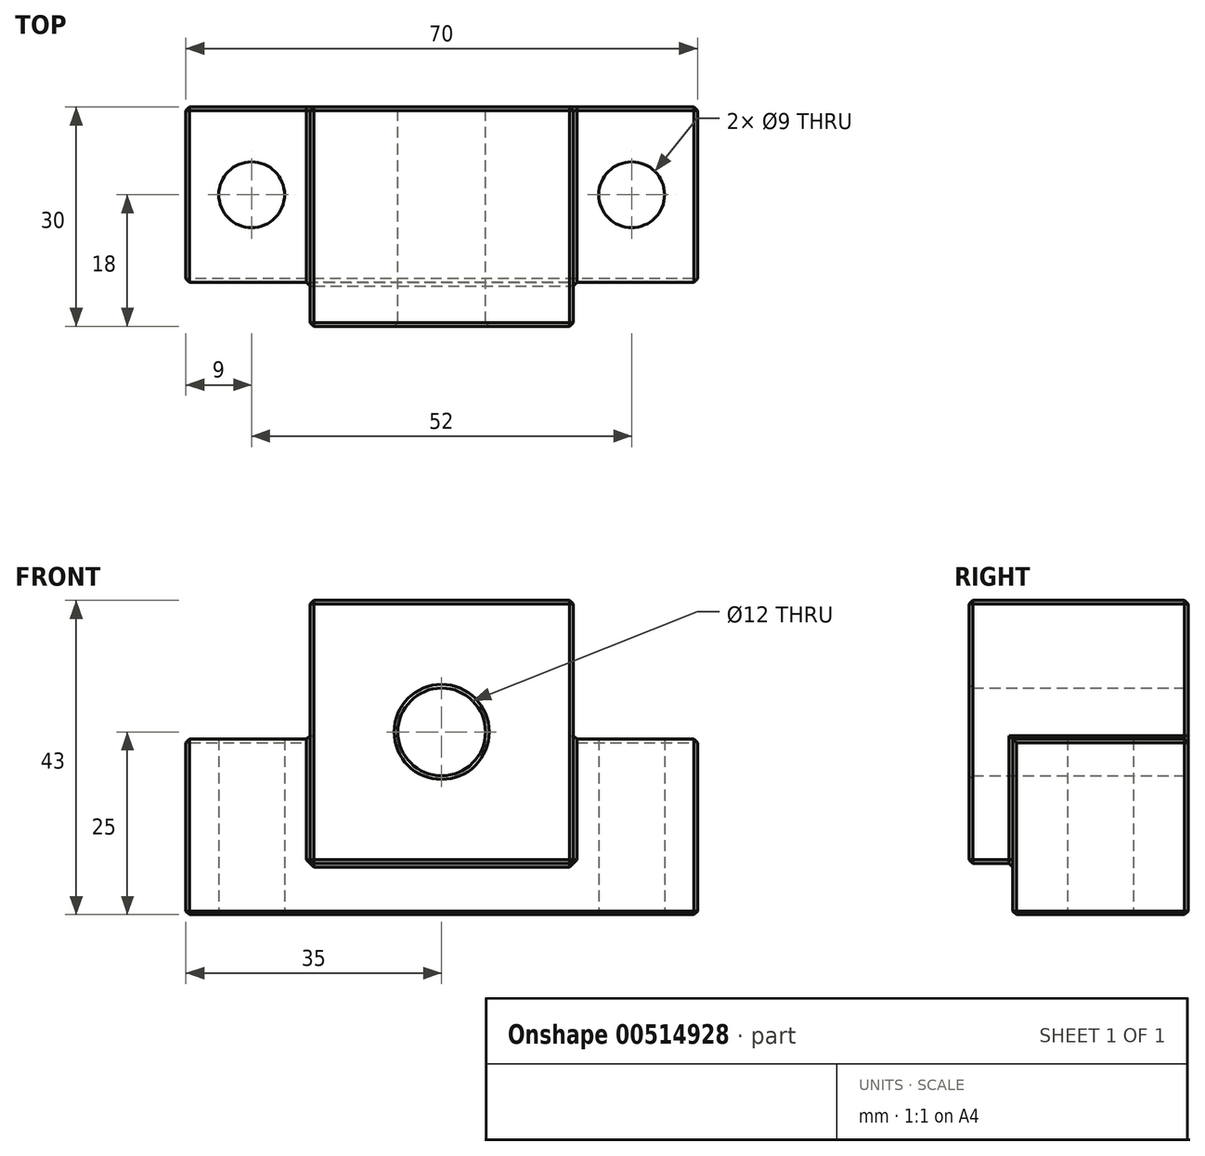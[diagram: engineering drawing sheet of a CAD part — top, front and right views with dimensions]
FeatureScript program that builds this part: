
annotation { "Feature Type Name" : "Feature", "Feature Type Description" : "" }
export const myFeature = defineFeature(function(context is Context, id is Id, definition is map)
    precondition{}
    {
        {
            var Q0;
            Q0=qCreatedBy(makeId("Front.planeOp"),FACE);
            var sketch = newSketch(context, id + "F0", { "sketchPlane" : qUnion([Q0])});
            skCircle(sketch, "E0", {"center": v(0, 0) * mm, "radius": 6 * mm});
            skLineSegment(sketch, "E1", {"start": v(0, 18) * mm, "end": v(18, 18) * mm});
            skLineSegment(sketch, "E2", {"start": v(18, 18) * mm, "end": v(18, -1) * mm});
            skLineSegment(sketch, "E3", {"start": v(18, -1) * mm, "end": v(35, -1) * mm});
            skLineSegment(sketch, "E4", {"start": v(35, -1) * mm, "end": v(35, -25) * mm});
            skLineSegment(sketch, "E5", {"start": v(35, -25) * mm, "end": v(0, -25) * mm});
            skLineSegment(sketch, "E6", {"start": v(0, 33.37) * mm, "end": v(0, -25.28) * mm, "construction": true});
            skCircle(sketch, "E7", {"center": v(0, 0) * mm, "radius": 9.5 * mm, "construction": true});
            skLineSegment(sketch, "E8.MirrorCS", {"start": v(0, 18) * mm, "end": v(-18, 18) * mm});
            skLineSegment(sketch, "E9.MirrorCS", {"start": v(-18, 18) * mm, "end": v(-18, -1) * mm});
            skLineSegment(sketch, "E10.MirrorCS", {"start": v(-18, -1) * mm, "end": v(-35, -1) * mm});
            skLineSegment(sketch, "E11.MirrorCS", {"start": v(-35, -1) * mm, "end": v(-35, -25) * mm});
            skLineSegment(sketch, "E12.MirrorCS", {"start": v(-35, -25) * mm, "end": v(0, -25) * mm});
            skSolve(sketch);
        }
        {
            var Q0;
            Q0=makeQuery(id+"F0.imprint","IMPRINT",FACE,{"disambiguationData":[TD([[makeQuery(id+"F0.imprint","IMPRINT",EDGE,{"derivedFrom":sQuery(id+"F0.wireOp",EDGE,"E0")}),-1.0]])]});
            extrude(context, id + "F1", {"entities" : qUnion([Q0]), "endBound" : BoundingType.SYMMETRIC, "depth" : 24 * mm, "offsetDistance" : 25 * mm});
        }
        {
            var Q0;
            Q0=makeQuery(id+"F1.opExtrude","CAP_FACE",FACE,{"disambiguationData":[OSD([sQuery(id+"F0.wireOp",EDGE,"E0"),sQuery(id+"F0.wireOp",EDGE,"E1"),sQuery(id+"F0.wireOp",EDGE,"E2"),sQuery(id+"F0.wireOp",EDGE,"E3"),sQuery(id+"F0.wireOp",EDGE,"E4"),sQuery(id+"F0.wireOp",EDGE,"E5"),sQuery(id+"F0.wireOp",EDGE,"E8.MirrorCS"),sQuery(id+"F0.wireOp",EDGE,"E9.MirrorCS"),sQuery(id+"F0.wireOp",EDGE,"E10.MirrorCS"),sQuery(id+"F0.wireOp",EDGE,"E11.MirrorCS"),sQuery(id+"F0.wireOp",EDGE,"E12.MirrorCS")])],"isStart":false});
            var sketch = newSketch(context, id + "F2", { "sketchPlane" : qUnion([Q0])});
            skLineSegment(sketch, "E13.bottom", {"start": v(-18, 18) * mm, "end": v(18, 18) * mm});
            skLineSegment(sketch, "E13.top", {"start": v(-18, -18) * mm, "end": v(18, -18) * mm});
            skLineSegment(sketch, "E13.left", {"start": v(-18, 18) * mm, "end": v(-18, -18) * mm});
            skLineSegment(sketch, "E13.right", {"start": v(18, 18) * mm, "end": v(18, -18) * mm});
            skSolve(sketch);
        }
        {
            var Q0;
            {var subQ3=sQuery(id+"F2.wireOp",EDGE,"E13.bottom");Q0=makeQuery(id+"F2.imprint","IMPRINT",FACE,{"disambiguationData":[TD([[makeQuery(id+"F2.imprint","IMPRINT",EDGE,{"derivedFrom":subQ3}),-1.0]])]});}
            extrude(context, id + "F3", {"entities" : qUnion([Q0]), "operationType" : NewBodyOperationType.ADD, "depth" : 6 * mm, "offsetDistance" : 25 * mm});
        }
        {
            var Q0;
            Q0=makeQuery(id+"F1.opExtrude","SWEPT_FACE",FACE,{"disambiguationData":[OSD([sQuery(id+"F0.wireOp",EDGE,"E5"),sQuery(id+"F0.wireOp",EDGE,"E12.MirrorCS")])]});
            var sketch = newSketch(context, id + "F4", { "sketchPlane" : qUnion([Q0])});
            skPoint(sketch, "E14", {"position": v(-26, 0) * mm});
            skPoint(sketch, "E15", {"position": v(26, 0) * mm});
            skSolve(sketch);
        }
        {
            var Q0;
            Q0=sQuery(id+"F4.wireOp",VERTEX,"E14");
            var Q1;
            Q1=sQuery(id+"F4.wireOp",VERTEX,"E15");
            var Q2;
            Q2=makeQuery(id+"F1.opExtrude","SWEPT_BODY",BODY,{"disambiguationData":[OSD([sQuery(id+"F0.wireOp",EDGE,"E0"),sQuery(id+"F0.wireOp",EDGE,"E1"),sQuery(id+"F0.wireOp",EDGE,"E2"),sQuery(id+"F0.wireOp",EDGE,"E3"),sQuery(id+"F0.wireOp",EDGE,"E4"),sQuery(id+"F0.wireOp",EDGE,"E5"),sQuery(id+"F0.wireOp",EDGE,"E8.MirrorCS"),sQuery(id+"F0.wireOp",EDGE,"E9.MirrorCS"),sQuery(id+"F0.wireOp",EDGE,"E10.MirrorCS"),sQuery(id+"F0.wireOp",EDGE,"E11.MirrorCS"),sQuery(id+"F0.wireOp",EDGE,"E12.MirrorCS")])]});
            hole(context, id + "F5", {"style" : HoleStyle.SIMPLE, "endStyle" : HoleEndStyle.THROUGH, "holeDiameter" : 9 * mm, "majorDiameter" : 5 * mm, "isTappedThrough" : true, "tappedDepth" : 12 * mm, "tapClearance" : 3, "locations" : qUnion([Q0, Q1]), "scope" : qUnion([Q2])});
        }
        {
            var Q0;
            Q0=makeQuery(id+"F3.boolean.opBoolean","MERGE",EDGE,{"derivedFrom":[makeQuery(id+"F1.opExtrude","SWEPT_EDGE",EDGE,{"disambiguationData":[OSD([sQuery(id+"F0.wireOp",EDGE,"E1"),sQuery(id+"F0.wireOp",EDGE,"E2")])]}),makeQuery(id+"F3.opExtrude","SWEPT_EDGE",EDGE,{"disambiguationData":[OSD([sQuery(id+"F2.wireOp",EDGE,"E13.bottom"),sQuery(id+"F2.wireOp",EDGE,"E13.right")])]})]});
            var Q1;
            Q1=makeQuery(id+"F3.boolean.opBoolean","MERGE",EDGE,{"derivedFrom":[makeQuery(id+"F1.opExtrude","SWEPT_EDGE",EDGE,{"disambiguationData":[OSD([sQuery(id+"F0.wireOp",EDGE,"E8.MirrorCS"),sQuery(id+"F0.wireOp",EDGE,"E9.MirrorCS")])]}),makeQuery(id+"F3.opExtrude","SWEPT_EDGE",EDGE,{"disambiguationData":[OSD([sQuery(id+"F2.wireOp",EDGE,"E13.bottom"),sQuery(id+"F2.wireOp",EDGE,"E13.left")])]})]});
            var Q2;
            Q2=makeQuery(id+"F3.opExtrude","CAP_EDGE",EDGE,{"disambiguationData":[OSD([sQuery(id+"F2.wireOp",EDGE,"E13.bottom")])],"isStart":false});
            var Q3;
            Q3=makeQuery(id+"F3.opExtrude","CAP_FACE",FACE,{"disambiguationData":[OSD([sQuery(id+"F0.wireOp",EDGE,"E0"),sQuery(id+"F2.wireOp",EDGE,"E13.bottom"),sQuery(id+"F2.wireOp",EDGE,"E13.top"),sQuery(id+"F2.wireOp",EDGE,"E13.left"),sQuery(id+"F2.wireOp",EDGE,"E13.right")])],"isStart":false});
            var Q4;
            Q4=makeQuery(id+"F1.opExtrude","SWEPT_FACE",FACE,{"disambiguationData":[OSD([sQuery(id+"F0.wireOp",EDGE,"E4")])]});
            var Q5;
            Q5=makeQuery(id+"F1.opExtrude","CAP_EDGE",EDGE,{"disambiguationData":[OSD([sQuery(id+"F0.wireOp",EDGE,"E3")])],"isStart":true});
            var Q6;
            Q6=makeQuery(id+"F1.opExtrude","CAP_EDGE",EDGE,{"disambiguationData":[OSD([sQuery(id+"F0.wireOp",EDGE,"E2")])],"isStart":true});
            var Q7;
            Q7=makeQuery(id+"F3.boolean.opBoolean","MERGE",FACE,{"derivedFrom":[makeQuery(id+"F1.opExtrude","SWEPT_FACE",FACE,{"disambiguationData":[OSD([sQuery(id+"F0.wireOp",EDGE,"E1"),sQuery(id+"F0.wireOp",EDGE,"E8.MirrorCS")])]}),makeQuery(id+"F3.opExtrude","SWEPT_FACE",FACE,{"disambiguationData":[OSD([sQuery(id+"F2.wireOp",EDGE,"E13.bottom")])]})]});
            var Q8;
            Q8=makeQuery(id+"F1.opExtrude","CAP_EDGE",EDGE,{"disambiguationData":[OSD([sQuery(id+"F0.wireOp",EDGE,"E10.MirrorCS")])],"isStart":true});
            var Q9;
            Q9=makeQuery(id+"F3.boolean.opBoolean","MERGE",FACE,{"derivedFrom":[makeQuery(id+"F1.opExtrude","SWEPT_FACE",FACE,{"disambiguationData":[OSD([sQuery(id+"F0.wireOp",EDGE,"E9.MirrorCS")])]}),makeQuery(id+"F3.opExtrude","SWEPT_FACE",FACE,{"disambiguationData":[OSD([sQuery(id+"F2.wireOp",EDGE,"E13.left")])]})]});
            var Q10;
            Q10=makeQuery(id+"F3.boolean.opBoolean","MERGE",FACE,{"derivedFrom":[makeQuery(id+"F1.opExtrude","SWEPT_FACE",FACE,{"disambiguationData":[OSD([sQuery(id+"F0.wireOp",EDGE,"E2")])]}),makeQuery(id+"F3.opExtrude","SWEPT_FACE",FACE,{"disambiguationData":[OSD([sQuery(id+"F2.wireOp",EDGE,"E13.right")])]})]});
            var Q11;
            Q11=makeQuery(id+"F1.opExtrude","CAP_EDGE",EDGE,{"disambiguationData":[OSD([sQuery(id+"F0.wireOp",EDGE,"E5"),sQuery(id+"F0.wireOp",EDGE,"E12.MirrorCS")])],"isStart":true});
            var Q12;
            Q12=makeQuery(id+"F1.opExtrude","SWEPT_FACE",FACE,{"disambiguationData":[OSD([sQuery(id+"F0.wireOp",EDGE,"E11.MirrorCS")])]});
            var Q13;
            Q13=makeQuery(id+"F1.opExtrude","CAP_EDGE",EDGE,{"disambiguationData":[OSD([sQuery(id+"F0.wireOp",EDGE,"E5"),sQuery(id+"F0.wireOp",EDGE,"E12.MirrorCS")])],"isStart":false});
            chamfer(context, id + "F6", {"entities" : qUnion([Q0, Q1, Q2, Q3, Q4, Q5, Q6, Q7, Q8, Q9, Q10, Q11, Q12, Q13]), "width" : 0.5 * mm, "tangentPropagation" : true});
        }
    });
